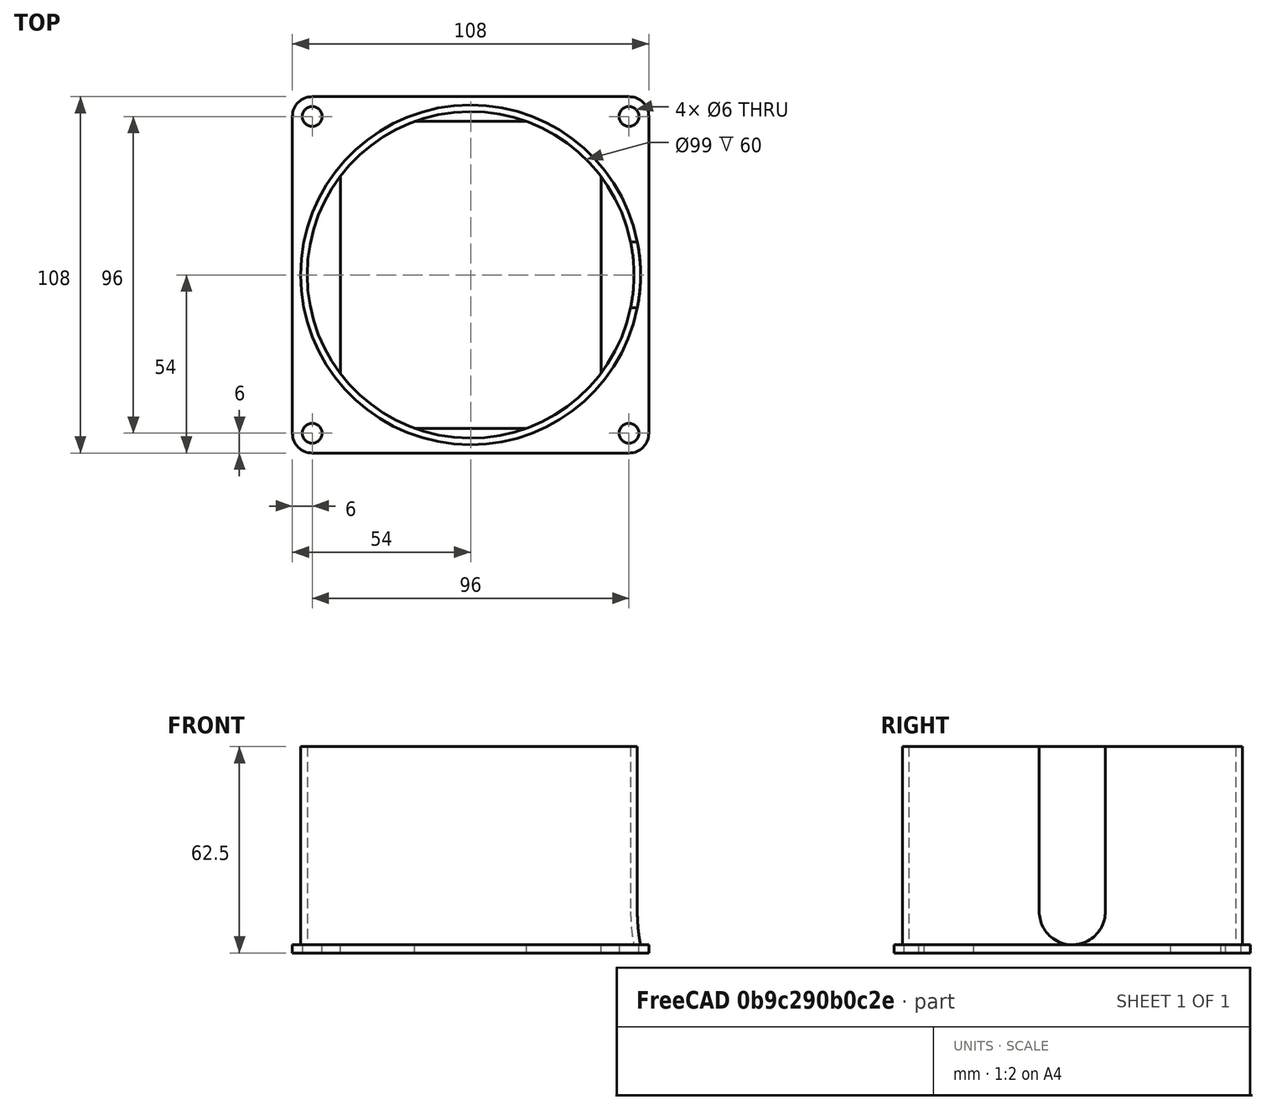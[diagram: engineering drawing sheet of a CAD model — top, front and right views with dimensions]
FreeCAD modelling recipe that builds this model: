
FCSTD DOCUMENT  (FreeCAD 0.18.4R)
Label: ringV6
License: All rights reserved
LicenseURL: http://en.wikipedia.org/wiki/All_rights_reserved
objects: Sketcher::SketchObject×4, PartDesign::Pad×2, PartDesign::Plane×1, PartDesign::Pocket×1, PartDesign::Body×1
note: 12 computed .brp shape members not serialized (recipe doc carries the construction recipe); baked Part::Feature solids carry a one-line shape summary decoded from their .brp

FEATURE [Sketcher::SketchObject] Sketch
  MapMode = 5
  Support = -> [XY_Plane]
  constraints (84):
    c: Horizontal(g0)
    c: Horizontal(g2)
    c: Vertical(g1)
    c: Vertical(g3)
    c: Equal(g1,g0)
    c: Coincident(g4,g-1)
    c: Equal(g8,g5)
    c: Equal(g5,g6)
    c: Equal(g6,g7)
    c: Vertical(g7,g6)
    c: Vertical(g8,g5)
    c: Horizontal(g5,g6)
    c: PointOnObject(g9,g4)
    c: PointOnObject(g9,g4)
    c: Vertical(g9)
    c: PointOnObject(g10,g4)
    c: PointOnObject(g10,g4)
    c: Vertical(g10)
    c: Horizontal(g11)
    c: Horizontal(g12)
    c: PointOnObject(g13,g11)
    c: Coincident(g13,g4)
    c: Vertical(g13)
    c: PointOnObject(g14,g12)
    c: Coincident(g14,g4)
    c: Vertical(g14)
    c: PointOnObject(g15,g9)
    c: Coincident(g15,g4)
    c: Horizontal(g15)
    c: Coincident(g16,g4)
    c: PointOnObject(g16,g10)
    c: Horizontal(g16)
    c: Equal(g15,g16)
    c: Equal(g13,g14)
    c: Diameter(g7) = 6
    c: Coincident(g17,g-1)
    c: Coincident(g17,g12)
    c: Coincident(g17,g10)
    c: Coincident(g18,g17)
    c: Coincident(g18,g12)
    c: Coincident(g18,g9)
    c: Coincident(g19,g17)
    c: Coincident(g19,g9)
    c: Coincident(g19,g11)
    c: Coincident(g20,g17)
    c: Coincident(g20,g11)
    c: Coincident(g20,g10)
    c: Distance(g7,g6) = 96
    c: Radius(g4) = 49.5
    c: Coincident(g21,g15)
    c: PointOnObject(g21,g4)
    c: Horizontal(g21)
    c: Distance(g21) = 10
    c: Coincident(g22,g13)
    c: PointOnObject(g22,g4)
    c: Vertical(g22)
    c: Distance(g22) = 3
    c: Tangent(g1,g23) = 1.5708
    c: Tangent(g2,g23) = 1.5708
    c: Coincident(g23,g7)
    c: Tangent(g0,g24) = 1.5708
    c: Tangent(g1,g24) = 1.5708
    c: Tangent(g0,g25) = 1.5708
    c: Tangent(g3,g25) = 1.5708
    c: Tangent(g2,g26) = 1.5708
    c: Tangent(g3,g26) = 1.5708
    c: DistanceY(g2,g0) = 108
    c: Coincident(g6,g24)
    c: Coincident(g5,g25)
    c: Coincident(g8,g26)
    c: PointOnObject(g27,g0)
    c: Vertical(g27)
    c: Coincident(g28,g27)
    c: PointOnObject(g28,g2)
    c: Vertical(g28)
    c: Equal(g28,g27)
    c: Coincident(g29,g27)
    c: PointOnObject(g29,g3)
    c: Horizontal(g29)
    c: Coincident(g30,g27)
    c: PointOnObject(g30,g1)
    c: Horizontal(g30)
    c: Equal(g30,g29)
    c: Coincident(g27,g17)
FEATURE [PartDesign::Pad] Pad
  Length = 2.5
  Length2 = 100
  Profile = -> Sketch
  Type = 0
FEATURE [PartDesign::Pad] Pad001  label="Unnamed"
  Length = 100
  Length2 = 100
  Type = 0
FEATURE [PartDesign::Plane] DatumPlane  label="Unnamed"
  Length = 24
  ResizeMode = 0
  Width = 24
FEATURE [Sketcher::SketchObject] Sketch001  label="Sketch005"
  ExternalGeometry = -> [Pad]
  MapMode = 5
  Placement = pos=(44.5,-1e-15,2.5) rot=(-0.57735,0.57735,0.57735;4.18879rad)
  Support = -> [DatumPlane]
  constraints (4):
    c: Coincident(g0,g-1)
    c: Coincident(g1,g0)
    c: PointOnObject(g-3,g1)
    c: Radius(g0) = 51.5
FEATURE [Sketcher::SketchObject] Sketch005  label="Unnamed"
FEATURE [Sketcher::SketchObject] Sketch006  label="Unnamed"
  constraints (7):
    c: Vertical(g0)
    c: Coincident(g0,g1)
    c: Coincident(g1,g2)
    c: Coincident(g2,g0)
    c: Horizontal(g2)
    c: Distance(g0) = 5
    c: Distance(g2) = 1
FEATURE [PartDesign::Pocket] Pocket  label="Unnamed"
  Length = 100
  Length2 = 100
  Type = 0
FEATURE [PartDesign::Body] Body
  Group = -> [Sketch,Pad,Sketch001,Pad001,DatumPlane,Sketch005,Sketch006,Pocket]
  Origin = -> Origin
  Tip = -> Pocket
